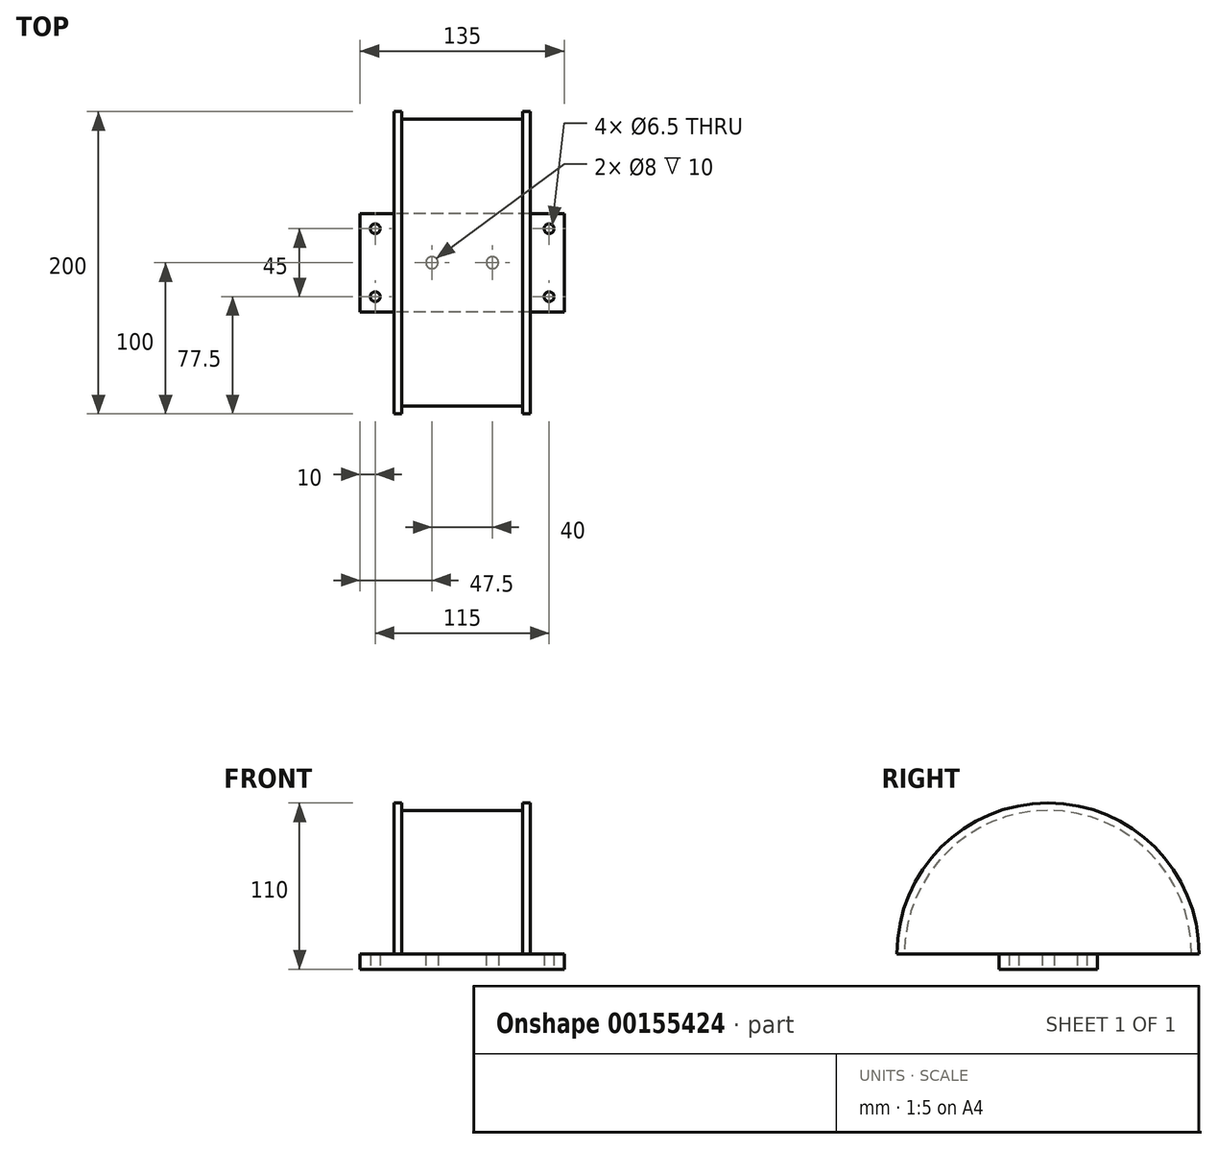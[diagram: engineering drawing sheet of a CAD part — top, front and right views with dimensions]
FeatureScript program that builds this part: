
annotation { "Feature Type Name" : "Feature", "Feature Type Description" : "" }
export const myFeature = defineFeature(function(context is Context, id is Id, definition is map)
    precondition{}
    {
        {
            var Q0;
            Q0=qCreatedBy(makeId("Top.planeOp"),FACE);
            var sketch = newSketch(context, id + "F0", { "sketchPlane" : qUnion([Q0])});
            skLineSegment(sketch, "E0.bottom", {"start": v(67.5, -32.5) * mm, "end": v(-67.5, -32.5) * mm});
            skLineSegment(sketch, "E0.top", {"start": v(67.5, 32.5) * mm, "end": v(-67.5, 32.5) * mm});
            skLineSegment(sketch, "E0.left", {"start": v(67.5, -32.5) * mm, "end": v(67.5, 32.5) * mm});
            skLineSegment(sketch, "E0.right", {"start": v(-67.5, -32.5) * mm, "end": v(-67.5, 32.5) * mm});
            skPoint(sketch, "E0.middle", {"position": v(0, 0) * mm});
            skCircle(sketch, "E1", {"center": v(-57.5, 22.5) * mm, "radius": 3.25 * mm});
            skCircle(sketch, "E2.MirrorC", {"center": v(57.5, 22.5) * mm, "radius": 3.25 * mm});
            skCircle(sketch, "E3.MirrorC", {"center": v(-57.5, -22.5) * mm, "radius": 3.25 * mm});
            skCircle(sketch, "E4.MirrorC", {"center": v(57.5, -22.5) * mm, "radius": 3.25 * mm});
            skCircle(sketch, "E5", {"center": v(-20, 0) * mm, "radius": 4 * mm});
            skCircle(sketch, "E6.MirrorC", {"center": v(20, 0) * mm, "radius": 4 * mm});
            skSolve(sketch);
        }
        {
            var Q0;
            Q0=makeQuery(id+"F0.imprint","IMPRINT",FACE,{"disambiguationData":[TD([[makeQuery(id+"F0.imprint","IMPRINT",EDGE,{"derivedFrom":sQuery(id+"F0.wireOp",EDGE,"E0.bottom")}),-1.0]])]});
            extrude(context, id + "F1", {"entities" : qUnion([Q0]), "depth" : 10 * mm});
        }
        {
            var Q0;
            Q0=makeQuery(id+"F1.opExtrude","CAP_FACE",FACE,{"disambiguationData":[OSD([sQuery(id+"F0.wireOp",EDGE,"E0.bottom"),sQuery(id+"F0.wireOp",EDGE,"E0.top"),sQuery(id+"F0.wireOp",EDGE,"E0.left"),sQuery(id+"F0.wireOp",EDGE,"E0.right"),sQuery(id+"F0.wireOp",EDGE,"E1"),sQuery(id+"F0.wireOp",EDGE,"E2.MirrorC"),sQuery(id+"F0.wireOp",EDGE,"E3.MirrorC"),sQuery(id+"F0.wireOp",EDGE,"E4.MirrorC"),sQuery(id+"F0.wireOp",EDGE,"E5"),sQuery(id+"F0.wireOp",EDGE,"E6.MirrorC")])],"isStart":false});
            var sketch = newSketch(context, id + "F2", { "sketchPlane" : qUnion([Q0])});
            skLineSegment(sketch, "E7.bottom", {"start": v(0, 0) * mm, "end": v(-40, 0) * mm});
            skLineSegment(sketch, "E7.top", {"start": v(0, -95) * mm, "end": v(-40, -95) * mm});
            skLineSegment(sketch, "E7.left", {"start": v(0, 0) * mm, "end": v(0, -95) * mm, "construction": true});
            skLineSegment(sketch, "E7.right", {"start": v(-40, 0) * mm, "end": v(-40, -95) * mm});
            skLineSegment(sketch, "E8.bottom", {"start": v(-40, 0) * mm, "end": v(-45, 0) * mm});
            skLineSegment(sketch, "E8.top", {"start": v(-40, -100) * mm, "end": v(-45, -100) * mm});
            skLineSegment(sketch, "E8.left", {"start": v(-40, 0) * mm, "end": v(-40, -100) * mm});
            skLineSegment(sketch, "E8.right", {"start": v(-45, 0) * mm, "end": v(-45, -100) * mm});
            skLineSegment(sketch, "E9.MirrorCS", {"start": v(-50, -100) * mm, "end": v(-45, -100) * mm});
            skLineSegment(sketch, "E10.MirrorCS", {"start": v(0, -95) * mm, "end": v(40, -95) * mm});
            skLineSegment(sketch, "E11.MirrorCS", {"start": v(40, 0) * mm, "end": v(40, -100) * mm});
            skLineSegment(sketch, "E12.MirrorCS", {"start": v(40, -100) * mm, "end": v(45, -100) * mm});
            skLineSegment(sketch, "E13.MirrorCS", {"start": v(45, 0) * mm, "end": v(45, -100) * mm});
            skLineSegment(sketch, "E14.MirrorCS", {"start": v(0, 0) * mm, "end": v(40, 0) * mm});
            skLineSegment(sketch, "E15.MirrorCS", {"start": v(40, 0) * mm, "end": v(45, 0) * mm});
            skLineSegment(sketch, "E16", {"start": v(-91.03, 0) * mm, "end": v(79.83, 0) * mm, "construction": true});
            skPoint(sketch, "E16.endSnap0", {"position": v(67.5, 0) * mm});
            skSolve(sketch);
        }
        {
            var Q0;
            Q0 = qSketchRegion(id + "F2", true);
            var Q1;
            Q1=sQuery(id+"F2.wireOp",EDGE,"E16");
            revolve(context, id + "F3", {"operationType" : NewBodyOperationType.ADD, "entities" : qUnion([Q0]), "axis" : qUnion([Q1]), "revolveType" : RevolveType.ONE_DIRECTION, "oppositeDirection" : true, "angle" : 180 * degree});
        }
    });
